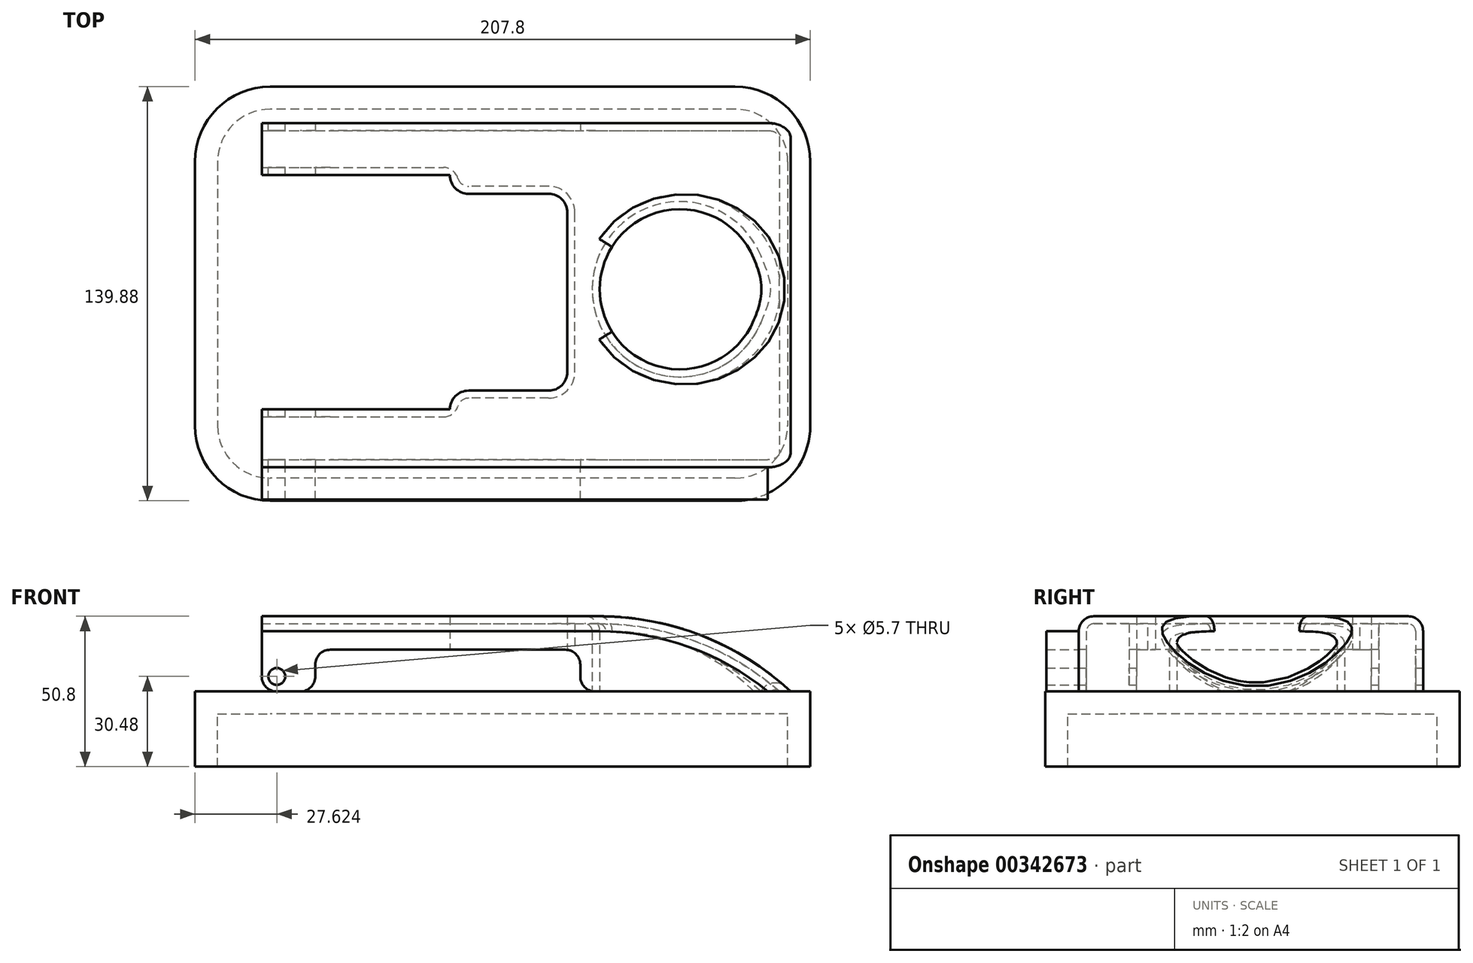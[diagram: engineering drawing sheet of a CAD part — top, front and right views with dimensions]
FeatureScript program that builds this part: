
annotation { "Feature Type Name" : "Feature", "Feature Type Description" : "" }
export const myFeature = defineFeature(function(context is Context, id is Id, definition is map)
    precondition{}
    {
        {
            var Q0;
            Q0=qCreatedBy(makeId("Top.planeOp"),FACE);
            var sketch = newSketch(context, id + "F0", { "sketchPlane" : qUnion([Q0])});
            skLineSegment(sketch, "E0.bottom", {"start": v(-56.99, 56.12) * mm, "end": v(58.14, 56.12) * mm});
            skLineSegment(sketch, "E0.top", {"start": v(-56.99, -60.15) * mm, "end": v(58.14, -60.15) * mm});
            skLineSegment(sketch, "E0.left", {"start": v(-56.99, 56.12) * mm, "end": v(-56.99, 38.58) * mm});
            skLineSegment(sketch, "E0.right", {"start": v(58.14, 56.12) * mm, "end": v(58.14, -60.15) * mm});
            skLineSegment(sketch, "E1.bottom", {"start": v(-50.64, 32.23) * mm, "end": v(-23.62, 32.23) * mm});
            skLineSegment(sketch, "E1.top", {"start": v(-50.64, -34.25) * mm, "end": v(-23.62, -34.25) * mm});
            skLineSegment(sketch, "E1.right", {"start": v(-17.27, 25.88) * mm, "end": v(-17.27, -27.9) * mm});
            skLineSegment(sketch, "E2.trimOffspring", {"start": v(-56.99, -40.6) * mm, "end": v(-56.99, -60.15) * mm});
            skPoint(sketch, "E3.visualSharp", {"position": v(-56.99, 32.23) * mm});
            skArc(sketch, "E3.filletArc", {"start": v(-56.99, 38.58) * mm, "mid": v(-55.13, 34.1) * mm, "end": v(-50.64, 32.23) * mm});
            skPoint(sketch, "E4.visualSharp", {"position": v(-56.99, -34.25) * mm});
            skArc(sketch, "E4.filletArc", {"start": v(-50.64, -34.25) * mm, "mid": v(-55.13, -36.1) * mm, "end": v(-56.99, -40.6) * mm});
            skPoint(sketch, "E5.visualSharp", {"position": v(-17.27, 32.23) * mm});
            skArc(sketch, "E5.filletArc", {"start": v(-17.27, 25.88) * mm, "mid": v(-19.13, 30.37) * mm, "end": v(-23.62, 32.23) * mm});
            skPoint(sketch, "E6.visualSharp", {"position": v(-17.27, -34.25) * mm});
            skArc(sketch, "E6.filletArc", {"start": v(-23.62, -34.25) * mm, "mid": v(-19.13, -32.39) * mm, "end": v(-17.27, -27.9) * mm});
            skCircle(sketch, "E7", {"center": v(20.72, 0) * mm, "radius": 27.06 * mm});
            skSolve(sketch);
        }
        {
            var Q0;
            Q0=makeQuery(id+"F0.imprint","IMPRINT",FACE,{"disambiguationData":[TD([[makeQuery(id+"F0.imprint","IMPRINT",EDGE,{"derivedFrom":sQuery(id+"F0.wireOp",EDGE,"E0.bottom")}),-1.0]])]});
            extrude(context, id + "F1", {"entities" : qUnion([Q0]), "depth" : 25.4 * mm});
        }
        {
            var Q0;
            Q0=makeQuery(id+"F1.opExtrude","CAP_EDGE",EDGE,{"disambiguationData":[OSD([sQuery(id+"F0.wireOp",EDGE,"E0.right")])],"isStart":false});
            fillet(context, id + "F2", {"entities" : qUnion([Q0]), "radius" : 95.05 * mm, "tangentPropagation" : true, "allowEdgeOverflow" : false});
        }
        {
            var Q0;
            Q0=makeQuery(id+"F2.opFillet","BLEND_EDGE",EDGE,{"blendedFrom":[makeQuery(id+"F1.opExtrude","CAP_EDGE",EDGE,{"disambiguationData":[OSD([sQuery(id+"F0.wireOp",EDGE,"E0.right")])],"isStart":false}),makeQuery(id+"F1.opExtrude","SWEPT_FACE",FACE,{"disambiguationData":[OSD([sQuery(id+"F0.wireOp",EDGE,"E7")])]})],"blendedInto":[makeQuery(id+"F1.opExtrude","SWEPT_FACE",FACE,{"disambiguationData":[OSD([sQuery(id+"F0.wireOp",EDGE,"E7")])]})]});
            var Q1;
            Q1=makeQuery(id+"F1.opExtrude","CAP_EDGE",EDGE,{"disambiguationData":[OSD([sQuery(id+"F0.wireOp",EDGE,"E0.top")])],"isStart":false});
            var Q2;
            Q2=makeQuery(id+"F1.opExtrude","CAP_EDGE",EDGE,{"disambiguationData":[OSD([sQuery(id+"F0.wireOp",EDGE,"E0.bottom")])],"isStart":false});
            fillet(context, id + "F3", {"entities" : qUnion([Q0, Q1, Q2]), "radius" : 5.08 * mm, "tangentPropagation" : true, "allowEdgeOverflow" : false});
        }
        {
            var Q0;
            Q0=makeQuery(id+"F1.opExtrude","SWEPT_FACE",FACE,{"disambiguationData":[OSD([sQuery(id+"F0.wireOp",EDGE,"E0.left")])]});
            var Q1;
            Q1=makeQuery(id+"F1.opExtrude","SWEPT_FACE",FACE,{"disambiguationData":[OSD([sQuery(id+"F0.wireOp",EDGE,"E2.trimOffspring")])]});
            extrude(context, id + "F4", {"entities" : qUnion([Q0, Q1]), "operationType" : NewBodyOperationType.ADD, "depth" : 63.5 * mm});
        }
        {
            var Q0;
            {var subQ0=sQuery(id+"F0.wireOp",EDGE,"E2.trimOffspring");var subQ1=sQuery(id+"F0.wireOp",EDGE,"E0.left");Q0=makeQuery(id+"F4.boolean.opBoolean","MERGE",FACE,{"derivedFrom":[makeQuery(id+"F1.opExtrude","CAP_FACE",FACE,{"disambiguationData":[OSD([sQuery(id+"F0.wireOp",EDGE,"E0.bottom"),sQuery(id+"F0.wireOp",EDGE,"E0.top"),subQ1,sQuery(id+"F0.wireOp",EDGE,"E0.right"),sQuery(id+"F0.wireOp",EDGE,"E1.bottom"),sQuery(id+"F0.wireOp",EDGE,"E1.top"),sQuery(id+"F0.wireOp",EDGE,"E1.right"),subQ0,sQuery(id+"F0.wireOp",EDGE,"E3.filletArc"),sQuery(id+"F0.wireOp",EDGE,"E4.filletArc"),sQuery(id+"F0.wireOp",EDGE,"E5.filletArc"),sQuery(id+"F0.wireOp",EDGE,"E6.filletArc"),sQuery(id+"F0.wireOp",EDGE,"E7")])],"isStart":true}),makeQuery(id+"F4.opExtrude","SWEPT_FACE",FACE,{"disambiguationData":[OSD([subQ1]),TDD([makeQuery(id+"F1.opExtrude","CAP_EDGE",EDGE,{"disambiguationData":[OSD([subQ1])],"isStart":true})])]}),makeQuery(id+"F4.opExtrude","SWEPT_FACE",FACE,{"disambiguationData":[OSD([subQ0]),TDD([makeQuery(id+"F1.opExtrude","CAP_EDGE",EDGE,{"disambiguationData":[OSD([subQ0])],"isStart":true})])]})]});}
            var Q1;
            Q1=makeQuery(id+"F4.opExtrude","CAP_FACE",FACE,{"disambiguationData":[OSD([sQuery(id+"F0.wireOp",EDGE,"E2.trimOffspring")])],"isStart":false});
            var Q2;
            Q2=makeQuery(id+"F4.opExtrude","CAP_FACE",FACE,{"disambiguationData":[OSD([sQuery(id+"F0.wireOp",EDGE,"E0.left")])],"isStart":false});
            shell(context, id + "F5", {"entities" : qUnion([Q0, Q1, Q2]), "thickness" : 2.54 * mm});
        }
        {
            var Q0;
            {var subQ0=sQuery(id+"F0.wireOp",EDGE,"E2.trimOffspring");Q0=makeQuery(id+"F5.opShell","OFFSET_EDGE",EDGE,{"disambiguationData":[OSD([subQ0]),TDD([makeQuery(id+"F4.opExtrude","CAP_EDGE",EDGE,{"disambiguationData":[OSD([subQ0]),TDD([makeQuery(id+"F1.opExtrude","CAP_EDGE",EDGE,{"disambiguationData":[OSD([subQ0])],"isStart":true})])],"isStart":false})])]});}
            var Q1;
            {var subQ0=sQuery(id+"F0.wireOp",EDGE,"E2.trimOffspring");Q1=makeQuery(id+"F4.opExtrude","CAP_EDGE",EDGE,{"disambiguationData":[OSD([subQ0]),TDD([makeQuery(id+"F1.opExtrude","CAP_EDGE",EDGE,{"disambiguationData":[OSD([subQ0])],"isStart":true})])],"isStart":false});}
            var Q2;
            {var subQ0=sQuery(id+"F0.wireOp",EDGE,"E0.left");Q2=makeQuery(id+"F5.opShell","OFFSET_EDGE",EDGE,{"disambiguationData":[OSD([subQ0]),TDD([makeQuery(id+"F4.opExtrude","CAP_EDGE",EDGE,{"disambiguationData":[OSD([subQ0]),TDD([makeQuery(id+"F1.opExtrude","CAP_EDGE",EDGE,{"disambiguationData":[OSD([subQ0])],"isStart":true})])],"isStart":false})])]});}
            var Q3;
            {var subQ0=sQuery(id+"F0.wireOp",EDGE,"E0.left");Q3=makeQuery(id+"F4.opExtrude","CAP_EDGE",EDGE,{"disambiguationData":[OSD([subQ0]),TDD([makeQuery(id+"F1.opExtrude","CAP_EDGE",EDGE,{"disambiguationData":[OSD([subQ0])],"isStart":true})])],"isStart":false});}
            fillet(context, id + "F6", {"entities" : qUnion([Q0, Q1, Q2, Q3]), "radius" : 5.08 * mm, "tangentPropagation" : true, "allowEdgeOverflow" : false});
        }
        {
            var Q0;
            {var subQ0=sQuery(id+"F0.wireOp",EDGE,"E0.left");var subQ1=sQuery(id+"F0.wireOp",EDGE,"E0.bottom");Q0=makeQuery(id+"F4.boolean.opBoolean","MERGE",FACE,{"derivedFrom":[makeQuery(id+"F1.opExtrude","SWEPT_FACE",FACE,{"disambiguationData":[OSD([subQ1])]}),makeQuery(id+"F4.opExtrude","SWEPT_FACE",FACE,{"disambiguationData":[OSD([subQ1,subQ0]),TDD([makeQuery(id+"F1.opExtrude","SWEPT_EDGE",EDGE,{"disambiguationData":[OSD([subQ1,subQ0])]})])]})]});}
            var sketch = newSketch(context, id + "F7", { "sketchPlane" : qUnion([Q0])});
            skCircle(sketch, "E8", {"center": v(115.4, 5.08) * mm, "radius": 2.85 * mm});
            skSolve(sketch);
        }
        {
            var Q0;
            Q0=makeQuery(id+"F7.imprint","IMPRINT",FACE,{"disambiguationData":[TD([[makeQuery(id+"F7.imprint","IMPRINT",EDGE,{"derivedFrom":sQuery(id+"F7.wireOp",EDGE,"E8")}),1.0]])]});
            extrude(context, id + "F8", {"entities" : qUnion([Q0]), "operationType" : NewBodyOperationType.REMOVE, "oppositeDirection" : true, "depth" : 123.19 * mm});
        }
        {
            var Q0;
            {var subQ0=sQuery(id+"F0.wireOp",EDGE,"E2.trimOffspring");var subQ1=sQuery(id+"F0.wireOp",EDGE,"E0.top");Q0=makeQuery(id+"F4.boolean.opBoolean","MERGE",FACE,{"derivedFrom":[makeQuery(id+"F1.opExtrude","SWEPT_FACE",FACE,{"disambiguationData":[OSD([subQ1])]}),makeQuery(id+"F4.opExtrude","SWEPT_FACE",FACE,{"disambiguationData":[OSD([subQ1,subQ0]),TDD([makeQuery(id+"F1.opExtrude","SWEPT_EDGE",EDGE,{"disambiguationData":[OSD([subQ1,subQ0])]})])]})]});}
            var sketch = newSketch(context, id + "F9", { "sketchPlane" : qUnion([Q0])});
            skLineSegment(sketch, "E9.bottom", {"start": v(-102.44, 14.1) * mm, "end": v(-12.93, 14.1) * mm});
            skLineSegment(sketch, "E9.top", {"start": v(-102.44, -17.84) * mm, "end": v(-12.93, -17.84) * mm});
            skLineSegment(sketch, "E9.left", {"start": v(-102.44, 14.1) * mm, "end": v(-102.44, -17.84) * mm});
            skLineSegment(sketch, "E9.right", {"start": v(-12.93, 14.1) * mm, "end": v(-12.93, -17.84) * mm});
            skSolve(sketch);
        }
        {
            var Q0;
            Q0 = qSketchRegion(id + "F9", true);
            extrude(context, id + "F10", {"entities" : qUnion([Q0]), "operationType" : NewBodyOperationType.REMOVE, "oppositeDirection" : true, "depth" : 186.18 * mm});
        }
        {
            var Q0;
            {var subQ0=sQuery(id+"F0.wireOp",EDGE,"E2.trimOffspring");var subQ1=sQuery(id+"F0.wireOp",EDGE,"E0.left");Q0=makeQuery(id+"F10.boolean.opBoolean","INTERSECT",EDGE,{"disambiguationData":[OD(1.0)],"derivedFrom":[makeQuery(id+"F4.boolean.opBoolean","MERGE",FACE,{"derivedFrom":[makeQuery(id+"F1.opExtrude","CAP_FACE",FACE,{"disambiguationData":[OSD([sQuery(id+"F0.wireOp",EDGE,"E0.bottom"),sQuery(id+"F0.wireOp",EDGE,"E0.top"),subQ1,sQuery(id+"F0.wireOp",EDGE,"E0.right"),sQuery(id+"F0.wireOp",EDGE,"E1.bottom"),sQuery(id+"F0.wireOp",EDGE,"E1.top"),sQuery(id+"F0.wireOp",EDGE,"E1.right"),subQ0,sQuery(id+"F0.wireOp",EDGE,"E3.filletArc"),sQuery(id+"F0.wireOp",EDGE,"E4.filletArc"),sQuery(id+"F0.wireOp",EDGE,"E5.filletArc"),sQuery(id+"F0.wireOp",EDGE,"E6.filletArc"),sQuery(id+"F0.wireOp",EDGE,"E7")])],"isStart":true}),makeQuery(id+"F4.opExtrude","SWEPT_FACE",FACE,{"disambiguationData":[OSD([subQ1]),TDD([makeQuery(id+"F1.opExtrude","CAP_EDGE",EDGE,{"disambiguationData":[OSD([subQ1])],"isStart":true})])]}),makeQuery(id+"F4.opExtrude","SWEPT_FACE",FACE,{"disambiguationData":[OSD([subQ0]),TDD([makeQuery(id+"F1.opExtrude","CAP_EDGE",EDGE,{"disambiguationData":[OSD([subQ0])],"isStart":true})])]})]}),makeQuery(id+"F10.opExtrude","SWEPT_FACE",FACE,{"disambiguationData":[OSD([sQuery(id+"F9.wireOp",EDGE,"E9.left")])]})]});}
            var Q1;
            {var subQ0=sQuery(id+"F0.wireOp",EDGE,"E2.trimOffspring");var subQ1=sQuery(id+"F0.wireOp",EDGE,"E0.left");var subQ2=sQuery(id+"F0.wireOp",EDGE,"E7");var subQ3=sQuery(id+"F0.wireOp",EDGE,"E6.filletArc");var subQ4=sQuery(id+"F0.wireOp",EDGE,"E5.filletArc");var subQ5=sQuery(id+"F0.wireOp",EDGE,"E4.filletArc");var subQ6=sQuery(id+"F0.wireOp",EDGE,"E3.filletArc");var subQ7=sQuery(id+"F0.wireOp",EDGE,"E1.right");var subQ8=sQuery(id+"F0.wireOp",EDGE,"E1.top");var subQ9=sQuery(id+"F0.wireOp",EDGE,"E1.bottom");var subQ10=sQuery(id+"F0.wireOp",EDGE,"E0.right");var subQ11=sQuery(id+"F0.wireOp",EDGE,"E0.top");var subQ12=sQuery(id+"F0.wireOp",EDGE,"E0.bottom");Q1=makeQuery(id+"F10.boolean.opBoolean","INTERSECT",EDGE,{"disambiguationData":[OD(0.0)],"derivedFrom":[makeQuery(id+"F5.opShell","OFFSET_FACE",FACE,{"disambiguationData":[OSD([subQ12,subQ11,subQ1,subQ10,subQ9,subQ8,subQ7,subQ0,subQ6,subQ5,subQ4,subQ3,subQ2]),TDD([makeQuery(id+"F4.boolean.opBoolean","MERGE",FACE,{"derivedFrom":[makeQuery(id+"F1.opExtrude","CAP_FACE",FACE,{"disambiguationData":[OSD([subQ12,subQ11,subQ1,subQ10,subQ9,subQ8,subQ7,subQ0,subQ6,subQ5,subQ4,subQ3,subQ2])],"isStart":true}),makeQuery(id+"F4.opExtrude","SWEPT_FACE",FACE,{"disambiguationData":[OSD([subQ1]),TDD([makeQuery(id+"F1.opExtrude","CAP_EDGE",EDGE,{"disambiguationData":[OSD([subQ1])],"isStart":true})])]}),makeQuery(id+"F4.opExtrude","SWEPT_FACE",FACE,{"disambiguationData":[OSD([subQ0]),TDD([makeQuery(id+"F1.opExtrude","CAP_EDGE",EDGE,{"disambiguationData":[OSD([subQ0])],"isStart":true})])]})]})]),OD(0.0)]}),makeQuery(id+"F10.opExtrude","SWEPT_FACE",FACE,{"disambiguationData":[OSD([sQuery(id+"F9.wireOp",EDGE,"E9.left")])]})]});}
            var Q2;
            {var subQ0=sQuery(id+"F0.wireOp",EDGE,"E2.trimOffspring");var subQ1=sQuery(id+"F0.wireOp",EDGE,"E0.left");var subQ2=sQuery(id+"F0.wireOp",EDGE,"E7");var subQ3=sQuery(id+"F0.wireOp",EDGE,"E6.filletArc");var subQ4=sQuery(id+"F0.wireOp",EDGE,"E5.filletArc");var subQ5=sQuery(id+"F0.wireOp",EDGE,"E4.filletArc");var subQ6=sQuery(id+"F0.wireOp",EDGE,"E3.filletArc");var subQ7=sQuery(id+"F0.wireOp",EDGE,"E1.right");var subQ8=sQuery(id+"F0.wireOp",EDGE,"E1.top");var subQ9=sQuery(id+"F0.wireOp",EDGE,"E1.bottom");var subQ10=sQuery(id+"F0.wireOp",EDGE,"E0.right");var subQ11=sQuery(id+"F0.wireOp",EDGE,"E0.top");var subQ12=sQuery(id+"F0.wireOp",EDGE,"E0.bottom");Q2=makeQuery(id+"F10.boolean.opBoolean","INTERSECT",EDGE,{"disambiguationData":[OD(1.0)],"derivedFrom":[makeQuery(id+"F5.opShell","OFFSET_FACE",FACE,{"disambiguationData":[OSD([subQ12,subQ11,subQ1,subQ10,subQ9,subQ8,subQ7,subQ0,subQ6,subQ5,subQ4,subQ3,subQ2]),TDD([makeQuery(id+"F4.boolean.opBoolean","MERGE",FACE,{"derivedFrom":[makeQuery(id+"F1.opExtrude","CAP_FACE",FACE,{"disambiguationData":[OSD([subQ12,subQ11,subQ1,subQ10,subQ9,subQ8,subQ7,subQ0,subQ6,subQ5,subQ4,subQ3,subQ2])],"isStart":true}),makeQuery(id+"F4.opExtrude","SWEPT_FACE",FACE,{"disambiguationData":[OSD([subQ1]),TDD([makeQuery(id+"F1.opExtrude","CAP_EDGE",EDGE,{"disambiguationData":[OSD([subQ1])],"isStart":true})])]}),makeQuery(id+"F4.opExtrude","SWEPT_FACE",FACE,{"disambiguationData":[OSD([subQ0]),TDD([makeQuery(id+"F1.opExtrude","CAP_EDGE",EDGE,{"disambiguationData":[OSD([subQ0])],"isStart":true})])]})]})]),OD(0.0)]}),makeQuery(id+"F10.opExtrude","SWEPT_FACE",FACE,{"disambiguationData":[OSD([sQuery(id+"F9.wireOp",EDGE,"E9.left")])]})]});}
            var Q3;
            {var subQ0=sQuery(id+"F0.wireOp",EDGE,"E2.trimOffspring");var subQ1=sQuery(id+"F0.wireOp",EDGE,"E0.left");Q3=makeQuery(id+"F10.boolean.opBoolean","INTERSECT",EDGE,{"disambiguationData":[OD(0.0)],"derivedFrom":[makeQuery(id+"F4.boolean.opBoolean","MERGE",FACE,{"derivedFrom":[makeQuery(id+"F1.opExtrude","CAP_FACE",FACE,{"disambiguationData":[OSD([sQuery(id+"F0.wireOp",EDGE,"E0.bottom"),sQuery(id+"F0.wireOp",EDGE,"E0.top"),subQ1,sQuery(id+"F0.wireOp",EDGE,"E0.right"),sQuery(id+"F0.wireOp",EDGE,"E1.bottom"),sQuery(id+"F0.wireOp",EDGE,"E1.top"),sQuery(id+"F0.wireOp",EDGE,"E1.right"),subQ0,sQuery(id+"F0.wireOp",EDGE,"E3.filletArc"),sQuery(id+"F0.wireOp",EDGE,"E4.filletArc"),sQuery(id+"F0.wireOp",EDGE,"E5.filletArc"),sQuery(id+"F0.wireOp",EDGE,"E6.filletArc"),sQuery(id+"F0.wireOp",EDGE,"E7")])],"isStart":true}),makeQuery(id+"F4.opExtrude","SWEPT_FACE",FACE,{"disambiguationData":[OSD([subQ1]),TDD([makeQuery(id+"F1.opExtrude","CAP_EDGE",EDGE,{"disambiguationData":[OSD([subQ1])],"isStart":true})])]}),makeQuery(id+"F4.opExtrude","SWEPT_FACE",FACE,{"disambiguationData":[OSD([subQ0]),TDD([makeQuery(id+"F1.opExtrude","CAP_EDGE",EDGE,{"disambiguationData":[OSD([subQ0])],"isStart":true})])]})]}),makeQuery(id+"F10.opExtrude","SWEPT_FACE",FACE,{"disambiguationData":[OSD([sQuery(id+"F9.wireOp",EDGE,"E9.left")])]})]});}
            var Q4;
            {var subQ0=sQuery(id+"F9.wireOp",EDGE,"E9.bottom");var subQ2=sQuery(id+"F0.wireOp",EDGE,"E0.top");var subQ4=makeQuery(id+"F1.opExtrude","SWEPT_FACE",FACE,{"disambiguationData":[OSD([subQ2])]});var subQ5=sQuery(id+"F9.wireOp",EDGE,"E9.left");Q4=makeQuery(id+"F10.boolean.opBoolean","COPY",EDGE,{"disambiguationData":[TD([subQ4])],"derivedFrom":makeQuery(id+"F10.opExtrude","SWEPT_EDGE",EDGE,{"disambiguationData":[OSD([subQ0,subQ5])]})});}
            var Q5;
            {var subQ0=sQuery(id+"F0.wireOp",EDGE,"E4.filletArc");var subQ1=sQuery(id+"F0.wireOp",EDGE,"E2.trimOffspring");var subQ2=sQuery(id+"F9.wireOp",EDGE,"E9.bottom");var subQ3=sQuery(id+"F9.wireOp",EDGE,"E9.left");Q5=makeQuery(id+"F10.boolean.opBoolean","COPY",EDGE,{"disambiguationData":[TD([makeQuery(id+"F4.opExtrude","SWEPT_FACE",FACE,{"disambiguationData":[OSD([subQ1,subQ0])]})])],"derivedFrom":makeQuery(id+"F10.opExtrude","SWEPT_EDGE",EDGE,{"disambiguationData":[OSD([subQ2,subQ3])]})});}
            var Q6;
            {var subQ0=sQuery(id+"F0.wireOp",EDGE,"E3.filletArc");var subQ1=sQuery(id+"F0.wireOp",EDGE,"E0.left");var subQ2=sQuery(id+"F9.wireOp",EDGE,"E9.bottom");var subQ3=sQuery(id+"F9.wireOp",EDGE,"E9.left");Q6=makeQuery(id+"F10.boolean.opBoolean","COPY",EDGE,{"disambiguationData":[TD([makeQuery(id+"F4.opExtrude","SWEPT_FACE",FACE,{"disambiguationData":[OSD([subQ1,subQ0])]})])],"derivedFrom":makeQuery(id+"F10.opExtrude","SWEPT_EDGE",EDGE,{"disambiguationData":[OSD([subQ2,subQ3])]})});}
            var Q7;
            {var subQ0=sQuery(id+"F9.wireOp",EDGE,"E9.bottom");var subQ2=sQuery(id+"F0.wireOp",EDGE,"E0.bottom");var subQ4=makeQuery(id+"F1.opExtrude","SWEPT_FACE",FACE,{"disambiguationData":[OSD([subQ2])]});var subQ5=sQuery(id+"F9.wireOp",EDGE,"E9.left");Q7=makeQuery(id+"F10.boolean.opBoolean","COPY",EDGE,{"disambiguationData":[TD([subQ4])],"derivedFrom":makeQuery(id+"F10.opExtrude","SWEPT_EDGE",EDGE,{"disambiguationData":[OSD([subQ0,subQ5])]})});}
            var Q8;
            {var subQ0=sQuery(id+"F0.wireOp",EDGE,"E2.trimOffspring");var subQ1=sQuery(id+"F0.wireOp",EDGE,"E0.left");Q8=makeQuery(id+"F10.boolean.opBoolean","INTERSECT",EDGE,{"disambiguationData":[OD(0.0)],"derivedFrom":[makeQuery(id+"F4.boolean.opBoolean","MERGE",FACE,{"derivedFrom":[makeQuery(id+"F1.opExtrude","CAP_FACE",FACE,{"disambiguationData":[OSD([sQuery(id+"F0.wireOp",EDGE,"E0.bottom"),sQuery(id+"F0.wireOp",EDGE,"E0.top"),subQ1,sQuery(id+"F0.wireOp",EDGE,"E0.right"),sQuery(id+"F0.wireOp",EDGE,"E1.bottom"),sQuery(id+"F0.wireOp",EDGE,"E1.top"),sQuery(id+"F0.wireOp",EDGE,"E1.right"),subQ0,sQuery(id+"F0.wireOp",EDGE,"E3.filletArc"),sQuery(id+"F0.wireOp",EDGE,"E4.filletArc"),sQuery(id+"F0.wireOp",EDGE,"E5.filletArc"),sQuery(id+"F0.wireOp",EDGE,"E6.filletArc"),sQuery(id+"F0.wireOp",EDGE,"E7")])],"isStart":true}),makeQuery(id+"F4.opExtrude","SWEPT_FACE",FACE,{"disambiguationData":[OSD([subQ1]),TDD([makeQuery(id+"F1.opExtrude","CAP_EDGE",EDGE,{"disambiguationData":[OSD([subQ1])],"isStart":true})])]}),makeQuery(id+"F4.opExtrude","SWEPT_FACE",FACE,{"disambiguationData":[OSD([subQ0]),TDD([makeQuery(id+"F1.opExtrude","CAP_EDGE",EDGE,{"disambiguationData":[OSD([subQ0])],"isStart":true})])]})]}),makeQuery(id+"F10.opExtrude","SWEPT_FACE",FACE,{"disambiguationData":[OSD([sQuery(id+"F9.wireOp",EDGE,"E9.right")])]})]});}
            var Q9;
            {var subQ0=sQuery(id+"F0.wireOp",EDGE,"E2.trimOffspring");var subQ1=sQuery(id+"F0.wireOp",EDGE,"E0.left");Q9=makeQuery(id+"F10.boolean.opBoolean","INTERSECT",EDGE,{"disambiguationData":[OD(1.0)],"derivedFrom":[makeQuery(id+"F4.boolean.opBoolean","MERGE",FACE,{"derivedFrom":[makeQuery(id+"F1.opExtrude","CAP_FACE",FACE,{"disambiguationData":[OSD([sQuery(id+"F0.wireOp",EDGE,"E0.bottom"),sQuery(id+"F0.wireOp",EDGE,"E0.top"),subQ1,sQuery(id+"F0.wireOp",EDGE,"E0.right"),sQuery(id+"F0.wireOp",EDGE,"E1.bottom"),sQuery(id+"F0.wireOp",EDGE,"E1.top"),sQuery(id+"F0.wireOp",EDGE,"E1.right"),subQ0,sQuery(id+"F0.wireOp",EDGE,"E3.filletArc"),sQuery(id+"F0.wireOp",EDGE,"E4.filletArc"),sQuery(id+"F0.wireOp",EDGE,"E5.filletArc"),sQuery(id+"F0.wireOp",EDGE,"E6.filletArc"),sQuery(id+"F0.wireOp",EDGE,"E7")])],"isStart":true}),makeQuery(id+"F4.opExtrude","SWEPT_FACE",FACE,{"disambiguationData":[OSD([subQ1]),TDD([makeQuery(id+"F1.opExtrude","CAP_EDGE",EDGE,{"disambiguationData":[OSD([subQ1])],"isStart":true})])]}),makeQuery(id+"F4.opExtrude","SWEPT_FACE",FACE,{"disambiguationData":[OSD([subQ0]),TDD([makeQuery(id+"F1.opExtrude","CAP_EDGE",EDGE,{"disambiguationData":[OSD([subQ0])],"isStart":true})])]})]}),makeQuery(id+"F10.opExtrude","SWEPT_FACE",FACE,{"disambiguationData":[OSD([sQuery(id+"F9.wireOp",EDGE,"E9.right")])]})]});}
            var Q10;
            {var subQ0=sQuery(id+"F9.wireOp",EDGE,"E9.bottom");var subQ2=sQuery(id+"F0.wireOp",EDGE,"E0.top");var subQ4=makeQuery(id+"F1.opExtrude","SWEPT_FACE",FACE,{"disambiguationData":[OSD([subQ2])]});var subQ5=sQuery(id+"F9.wireOp",EDGE,"E9.right");Q10=makeQuery(id+"F10.boolean.opBoolean","COPY",EDGE,{"disambiguationData":[TD([subQ4])],"derivedFrom":makeQuery(id+"F10.opExtrude","SWEPT_EDGE",EDGE,{"disambiguationData":[OSD([subQ0,subQ5])]})});}
            var Q11;
            {var subQ0=sQuery(id+"F9.wireOp",EDGE,"E9.bottom");var subQ2=sQuery(id+"F0.wireOp",EDGE,"E0.bottom");var subQ4=makeQuery(id+"F1.opExtrude","SWEPT_FACE",FACE,{"disambiguationData":[OSD([subQ2])]});var subQ5=sQuery(id+"F9.wireOp",EDGE,"E9.right");Q11=makeQuery(id+"F10.boolean.opBoolean","COPY",EDGE,{"disambiguationData":[TD([subQ4])],"derivedFrom":makeQuery(id+"F10.opExtrude","SWEPT_EDGE",EDGE,{"disambiguationData":[OSD([subQ0,subQ5])]})});}
            fillet(context, id + "F11", {"entities" : qUnion([Q0, Q1, Q2, Q3, Q4, Q5, Q6, Q7, Q8, Q9, Q10, Q11]), "radius" : 5.08 * mm, "tangentPropagation" : true, "allowEdgeOverflow" : false});
        }
        {
            var Q0;
            {var subQ0=sQuery(id+"F0.wireOp",EDGE,"E3.filletArc");var subQ1=sQuery(id+"F0.wireOp",EDGE,"E0.left");Q0=makeQuery(id+"F5.opShell","OFFSET_EDGE",EDGE,{"disambiguationData":[OSD([subQ1,subQ0]),TDD([makeQuery(id+"F4.boolean.opBoolean","MERGE",EDGE,{"derivedFrom":[makeQuery(id+"F1.opExtrude","SWEPT_EDGE",EDGE,{"disambiguationData":[OSD([subQ1,subQ0])]}),makeQuery(id+"F4.opExtrude","CAP_EDGE",EDGE,{"disambiguationData":[OSD([subQ1,subQ0])],"isStart":true})]})])]});}
            var Q1;
            {var subQ0=sQuery(id+"F0.wireOp",EDGE,"E4.filletArc");var subQ1=sQuery(id+"F0.wireOp",EDGE,"E2.trimOffspring");Q1=makeQuery(id+"F5.opShell","OFFSET_EDGE",EDGE,{"disambiguationData":[OSD([subQ1,subQ0]),TDD([makeQuery(id+"F4.boolean.opBoolean","MERGE",EDGE,{"derivedFrom":[makeQuery(id+"F1.opExtrude","SWEPT_EDGE",EDGE,{"disambiguationData":[OSD([subQ1,subQ0])]}),makeQuery(id+"F4.opExtrude","CAP_EDGE",EDGE,{"disambiguationData":[OSD([subQ1,subQ0])],"isStart":true})]})])]});}
            fillet(context, id + "F12", {"entities" : qUnion([Q0, Q1]), "radius" : 5.08 * mm, "tangentPropagation" : true, "allowEdgeOverflow" : false});
        }
        {
            var Q0;
            Q0=qCreatedBy(makeId("Top.planeOp"),FACE);
            var sketch = newSketch(context, id + "F13", { "sketchPlane" : qUnion([Q0])});
            skLineSegment(sketch, "E10.bottom", {"start": v(64.77, 68.44) * mm, "end": v(-143.03, 68.44) * mm});
            skLineSegment(sketch, "E10.top", {"start": v(64.77, -71.44) * mm, "end": v(-143.03, -71.44) * mm});
            skLineSegment(sketch, "E10.left", {"start": v(64.77, 68.44) * mm, "end": v(64.77, -71.44) * mm});
            skLineSegment(sketch, "E10.right", {"start": v(-143.03, 68.44) * mm, "end": v(-143.03, -71.44) * mm});
            skSolve(sketch);
        }
        {
            var Q0;
            Q0 = qSketchRegion(id + "F13", true);
            extrude(context, id + "F14", {"entities" : qUnion([Q0]), "oppositeDirection" : true, "depth" : 25.4 * mm});
        }
        {
            var Q0;
            Q0=makeQuery(id+"F14.opExtrude","SWEPT_EDGE",EDGE,{"disambiguationData":[OSD([sQuery(id+"F13.wireOp",EDGE,"E10.top"),sQuery(id+"F13.wireOp",EDGE,"E10.left")])]});
            var Q1;
            Q1=makeQuery(id+"F14.opExtrude","SWEPT_EDGE",EDGE,{"disambiguationData":[OSD([sQuery(id+"F13.wireOp",EDGE,"E10.bottom"),sQuery(id+"F13.wireOp",EDGE,"E10.left")])]});
            var Q2;
            Q2=makeQuery(id+"F14.opExtrude","SWEPT_EDGE",EDGE,{"disambiguationData":[OSD([sQuery(id+"F13.wireOp",EDGE,"E10.top"),sQuery(id+"F13.wireOp",EDGE,"E10.right")])]});
            var Q3;
            Q3=makeQuery(id+"F14.opExtrude","SWEPT_EDGE",EDGE,{"disambiguationData":[OSD([sQuery(id+"F13.wireOp",EDGE,"E10.bottom"),sQuery(id+"F13.wireOp",EDGE,"E10.right")])]});
            fillet(context, id + "F15", {"entities" : qUnion([Q0, Q1, Q2, Q3]), "radius" : 25.4 * mm, "tangentPropagation" : true, "allowEdgeOverflow" : false});
        }
        {
            var Q0;
            {var subQ0=sQuery(id+"F0.wireOp",EDGE,"E2.trimOffspring");var subQ1=sQuery(id+"F0.wireOp",EDGE,"E0.top");Q0=makeQuery(id+"F4.boolean.opBoolean","MERGE",FACE,{"derivedFrom":[makeQuery(id+"F1.opExtrude","SWEPT_FACE",FACE,{"disambiguationData":[OSD([subQ1])]}),makeQuery(id+"F4.opExtrude","SWEPT_FACE",FACE,{"disambiguationData":[OSD([subQ1,subQ0]),TDD([makeQuery(id+"F1.opExtrude","SWEPT_EDGE",EDGE,{"disambiguationData":[OSD([subQ1,subQ0])]})])]})]});}
            extrude(context, id + "F16", {"entities" : qUnion([Q0]), "depth" : 10.92 * mm});
        }
        {
            var Q0;
            Q0=makeQuery(id+"F14.opExtrude","CAP_FACE",FACE,{"disambiguationData":[OSD([sQuery(id+"F13.wireOp",EDGE,"E10.bottom"),sQuery(id+"F13.wireOp",EDGE,"E10.top"),sQuery(id+"F13.wireOp",EDGE,"E10.left"),sQuery(id+"F13.wireOp",EDGE,"E10.right")])],"isStart":false});
            shell(context, id + "F17", {"entities" : qUnion([Q0]), "thickness" : 7.62 * mm});
        }
    });
